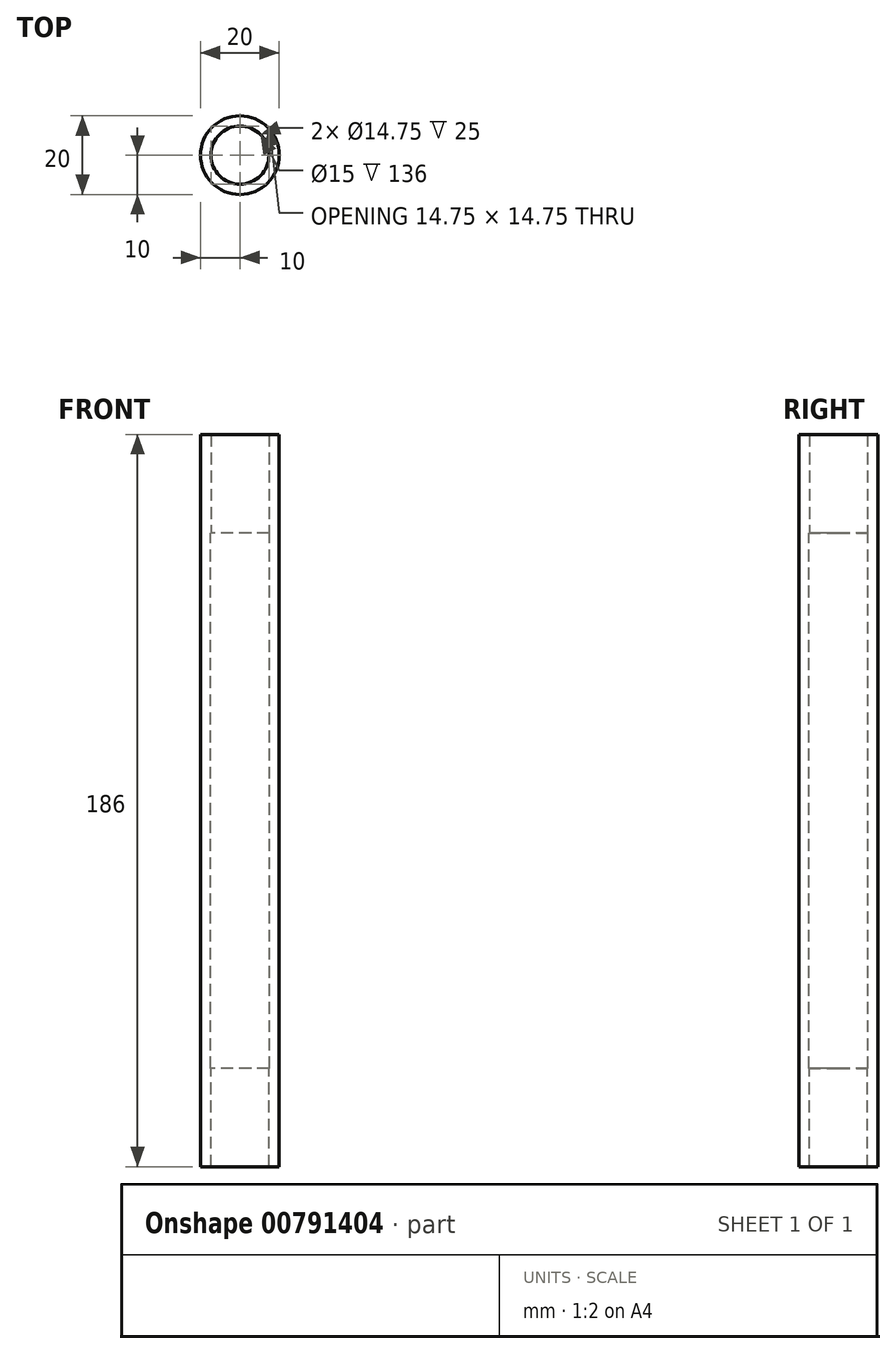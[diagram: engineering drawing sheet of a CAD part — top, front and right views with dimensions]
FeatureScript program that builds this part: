
annotation { "Feature Type Name" : "Feature", "Feature Type Description" : "" }
export const myFeature = defineFeature(function(context is Context, id is Id, definition is map)
    precondition{}
    {
        {
            var Q0;
            Q0=qCreatedBy(makeId("Top.planeOp"),FACE);
            var sketch = newSketch(context, id + "F0", { "sketchPlane" : qUnion([Q0])});
            skCircle(sketch, "E0", {"center": v(0, 0) * mm, "radius": 10 * mm});
            skSolve(sketch);
        }
        {
            var Q0;
            Q0 = qSketchRegion(id + "F0", true);
            extrude(context, id + "F1", {"entities" : qUnion([Q0]), "depth" : 186 * mm, "offsetDistance" : 25 * mm, "symmetric" : true});
        }
        {
            var Q0;
            Q0=makeQuery(id+"F1.opExtrude","CAP_FACE",FACE,{"disambiguationData":[OSD([sQuery(id+"F0.wireOp",EDGE,"E0")])],"isStart":true});
            var sketch = newSketch(context, id + "F2", { "sketchPlane" : qUnion([Q0])});
            skPoint(sketch, "E1", {"position": v(0, 0) * mm});
            skSolve(sketch);
        }
        {
            var Q0;
            Q0=makeQuery(id+"F1.opExtrude","CAP_FACE",FACE,{"disambiguationData":[OSD([sQuery(id+"F0.wireOp",EDGE,"E0")])],"isStart":false});
            var sketch = newSketch(context, id + "F3", { "sketchPlane" : qUnion([Q0])});
            skPoint(sketch, "E2", {"position": v(0, 0) * mm});
            skSolve(sketch);
        }
        {
            var Q0;
            Q0=sQuery(id+"F3.wireOp",VERTEX,"E2");
            var Q1;
            Q1=sQuery(id+"F2.wireOp",VERTEX,"E1");
            var Q2;
            Q2=makeQuery(id+"F1.opExtrude","SWEPT_BODY",BODY,{"disambiguationData":[OSD([sQuery(id+"F0.wireOp",EDGE,"E0")])]});
            hole(context, id + "F4", {"style" : HoleStyle.SIMPLE, "endStyle" : HoleEndStyle.BLIND, "standardTappedOrClearance" : lookupTablePath({ "standard" : "ISO", "engagement" : "50%", "pitch" : "2 mm", "size" : "M16", "type" : "Tapped" }), "standardBlindInLast" : lookupTablePath({ "standard" : "ISO", "fit" : "Normal", "engagement" : "50%", "pitch" : "2 mm", "size" : "M16", "type" : "Clearance & tapped" }), "holeDiameter" : 14.75 * mm, "majorDiameter" : 16 * mm, "showTappedDepth" : true, "holeDepth" : 31 * mm, "isTappedThrough" : true, "tappedDepth" : 25 * mm, "tapClearance" : 3, "locations" : qUnion([Q0, Q1]), "scope" : qUnion([Q2]), "startStyle" : HoleStartStyle.PART});
        }
        {
            var Q0;
            Q0=qCreatedBy(makeId("Top.planeOp"),FACE);
            var sketch = newSketch(context, id + "F5", { "sketchPlane" : qUnion([Q0])});
            skCircle(sketch, "E3", {"center": v(0, 0) * mm, "radius": 7.5 * mm});
            skSolve(sketch);
        }
        {
            var Q0;
            Q0 = qSketchRegion(id + "F5", true);
            extrude(context, id + "F6", {"entities" : qUnion([Q0]), "operationType" : NewBodyOperationType.REMOVE, "oppositeDirection" : true, "depth" : (186 - 2 * 25) * mm, "offsetDistance" : 25 * mm, "symmetric" : true});
        }
    });
